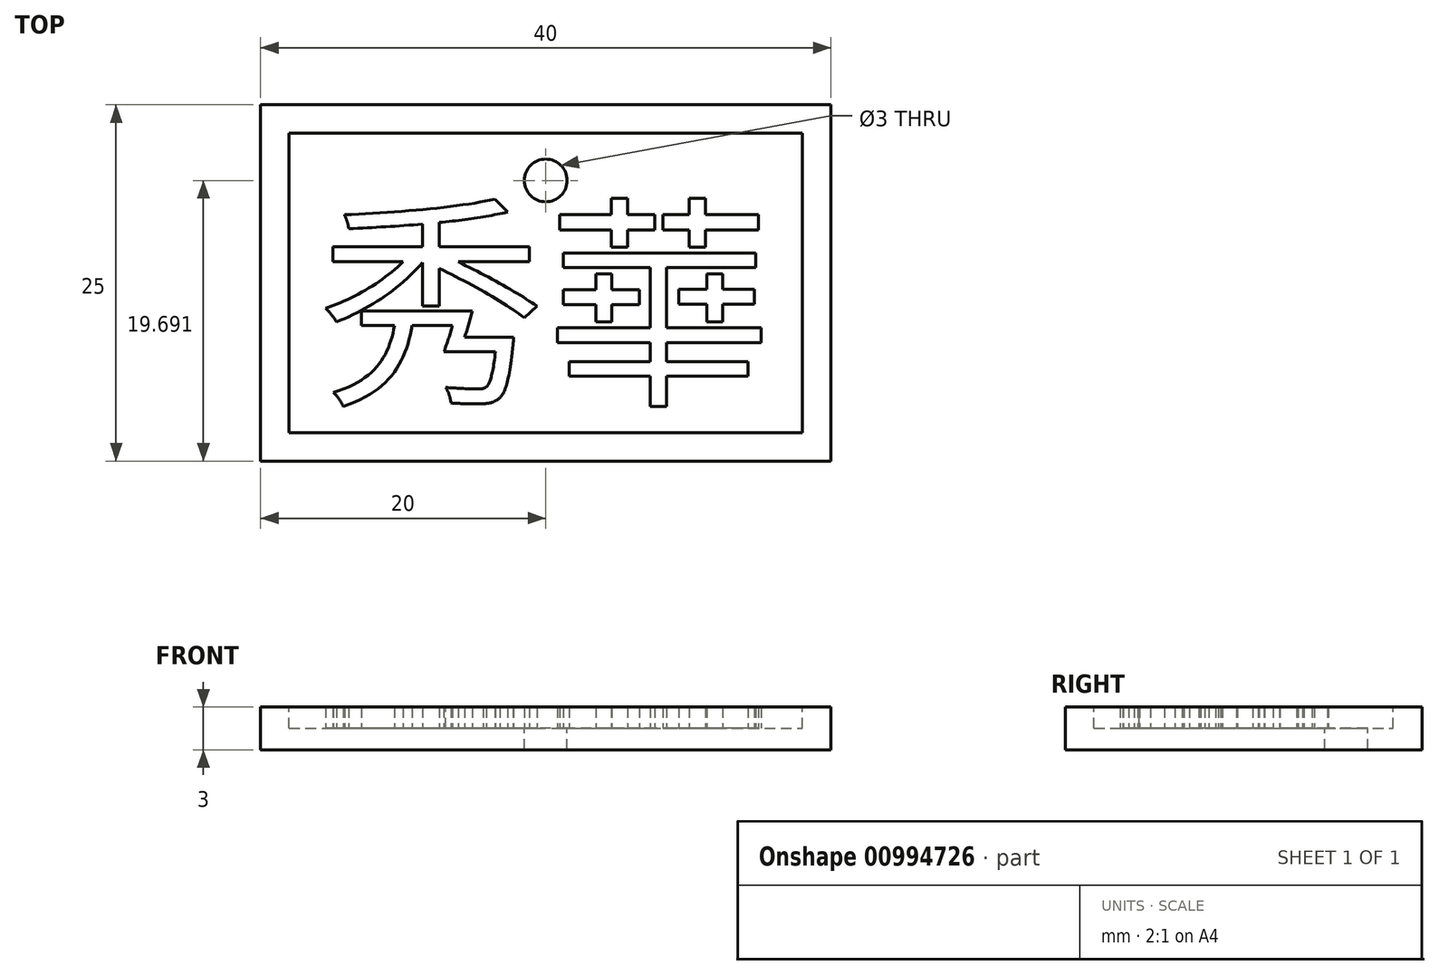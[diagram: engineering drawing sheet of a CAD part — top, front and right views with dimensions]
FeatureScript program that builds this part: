
annotation { "Feature Type Name" : "Feature", "Feature Type Description" : "" }
export const myFeature = defineFeature(function(context is Context, id is Id, definition is map)
    precondition{}
    {
        {
            var Q0;
            Q0=qCreatedBy(makeId("Top.planeOp"),FACE);
            var sketch = newSketch(context, id + "F0", { "sketchPlane" : qUnion([Q0])});
            skLineSegment(sketch, "E0.bottom", {"start": v(20, -12.5) * mm, "end": v(-20, -12.5) * mm});
            skLineSegment(sketch, "E0.top", {"start": v(20, 12.5) * mm, "end": v(-20, 12.5) * mm});
            skLineSegment(sketch, "E0.left", {"start": v(20, -12.5) * mm, "end": v(20, 12.5) * mm});
            skLineSegment(sketch, "E0.right", {"start": v(-20, -12.5) * mm, "end": v(-20, 12.5) * mm});
            skPoint(sketch, "E0.middle", {"position": v(0, 0) * mm});
            skSolve(sketch);
        }
        {
            var Q0;
            Q0 = qSketchRegion(id + "F0", true);
            extrude(context, id + "F1", {"entities" : qUnion([Q0]), "depth" : 3 * mm, "offsetDistance" : 25 * mm});
        }
        {
            var Q0;
            Q0=makeQuery(id+"F1.opExtrude","CAP_FACE",FACE,{"disambiguationData":[OSD([sQuery(id+"F0.wireOp",EDGE,"E0.bottom"),sQuery(id+"F0.wireOp",EDGE,"E0.top"),sQuery(id+"F0.wireOp",EDGE,"E0.left"),sQuery(id+"F0.wireOp",EDGE,"E0.right")])],"isStart":false});
            var sketch = newSketch(context, id + "F2", { "sketchPlane" : qUnion([Q0])});
            skLineSegment(sketch, "E1.0", {"start": v(18, -10.5) * mm, "end": v(18, 10.5) * mm});
            skLineSegment(sketch, "E1.1", {"start": v(-18, -10.5) * mm, "end": v(18, -10.5) * mm});
            skLineSegment(sketch, "E1.2", {"start": v(-18, 10.5) * mm, "end": v(-18, -10.5) * mm});
            skLineSegment(sketch, "E1.3", {"start": v(18, 10.5) * mm, "end": v(-18, 10.5) * mm});
            skSolve(sketch);
        }
        {
            var Q0;
            Q0 = qSketchRegion(id + "F2", true);
            extrude(context, id + "F3", {"entities" : qUnion([Q0]), "operationType" : NewBodyOperationType.REMOVE, "oppositeDirection" : true, "depth" : 1.5 * mm, "offsetDistance" : 25 * mm});
        }
        {
            var Q0;
            Q0=makeQuery(id+"F3.boolean.opBoolean","COPY",FACE,{"derivedFrom":makeQuery(id+"F3.opExtrude","CAP_FACE",FACE,{"disambiguationData":[OSD([sQuery(id+"F2.wireOp",EDGE,"E1.0"),sQuery(id+"F2.wireOp",EDGE,"E1.1"),sQuery(id+"F2.wireOp",EDGE,"E1.2"),sQuery(id+"F2.wireOp",EDGE,"E1.3")])],"isStart":false})});
            var sketch = newSketch(context, id + "F4", { "sketchPlane" : qUnion([Q0])});
            skCircle(sketch, "E2", {"center": v(0, 7.2) * mm, "radius": 1.5 * mm});
            skSolve(sketch);
        }
        {
            var Q0;
            Q0 = qSketchRegion(id + "F4", true);
            extrude(context, id + "F5", {"entities" : qUnion([Q0]), "operationType" : NewBodyOperationType.REMOVE, "endBound" : BoundingType.THROUGH_ALL, "oppositeDirection" : true, "depth" : 25 * mm, "offsetDistance" : 25 * mm});
        }
        {
            var Q0;
            Q0=makeQuery(id+"F3.boolean.opBoolean","COPY",FACE,{"derivedFrom":makeQuery(id+"F3.opExtrude","CAP_FACE",FACE,{"disambiguationData":[OSD([sQuery(id+"F2.wireOp",EDGE,"E1.0"),sQuery(id+"F2.wireOp",EDGE,"E1.1"),sQuery(id+"F2.wireOp",EDGE,"E1.2"),sQuery(id+"F2.wireOp",EDGE,"E1.3")])],"isStart":false})});
            var sketch = newSketch(context, id + "F6", { "sketchPlane" : qUnion([Q0])});
            skText(sketch, "E3", { "text": "秀華", "fontName": "NotoSansCJKtc-Regular.otf"});
            const initialGuessF6  = {"E3": [-0.016, -0.00742, 1, 0, 0.0115]};
            skSetInitialGuess(sketch, initialGuessF6);
            skSolve(sketch);
        }
        {
            var Q0;
            Q0 = qSketchRegion(id + "F6", true);
            extrude(context, id + "F7", {"entities" : qUnion([Q0]), "operationType" : NewBodyOperationType.ADD, "depth" : 1.5 * mm, "offsetDistance" : 25 * mm});
        }
    });
